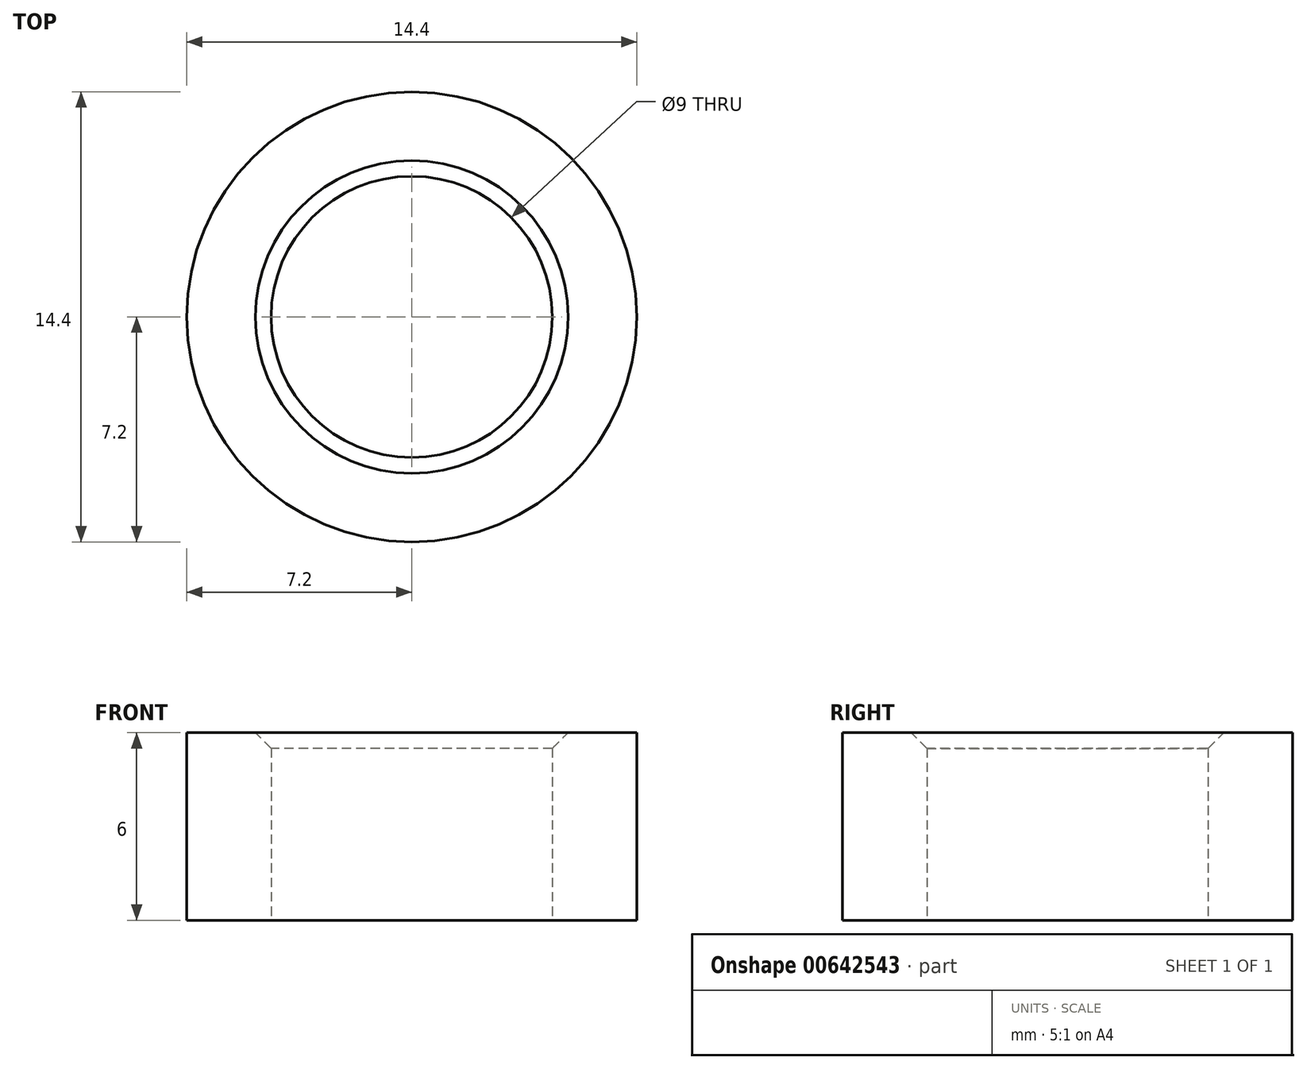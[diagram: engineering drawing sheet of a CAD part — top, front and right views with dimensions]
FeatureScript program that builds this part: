
annotation { "Feature Type Name" : "Feature", "Feature Type Description" : "" }
export const myFeature = defineFeature(function(context is Context, id is Id, definition is map)
    precondition{}
    {
        {
            var Q0;
            Q0=qCreatedBy(makeId("Top.planeOp"),FACE);
            var sketch = newSketch(context, id + "F0", { "sketchPlane" : qUnion([Q0])});
            skCircle(sketch, "E0", {"center": v(0, 0) * mm, "radius": 7.2 * mm});
            skCircle(sketch, "E1", {"center": v(0, 0) * mm, "radius": 4.5 * mm});
            skCircle(sketch, "E2", {"center": v(0, 0) * mm, "radius": 3.5 * mm});
            skSolve(sketch);
        }
        {
            var Q0;
            Q0 = qSketchRegion(id + "F0", true);
            extrude(context, id + "F1", {"entities" : qUnion([Q0]), "depth" : 6 * mm, "offsetDistance" : 25.4 * mm});
        }
        {
            var Q0;
            Q0=makeQuery(id+"F1.opExtrude","CAP_EDGE",EDGE,{"disambiguationData":[OSD([sQuery(id+"F0.wireOp",EDGE,"E1")])],"isStart":false});
            chamfer(context, id + "F2", {"entities" : qUnion([Q0]), "chamferType" : ChamferType.OFFSET_ANGLE, "width" : 0.5 * mm, "oppositeDirection" : false, "angle" : 45 * degree, "tangentPropagation" : true});
        }
    });
